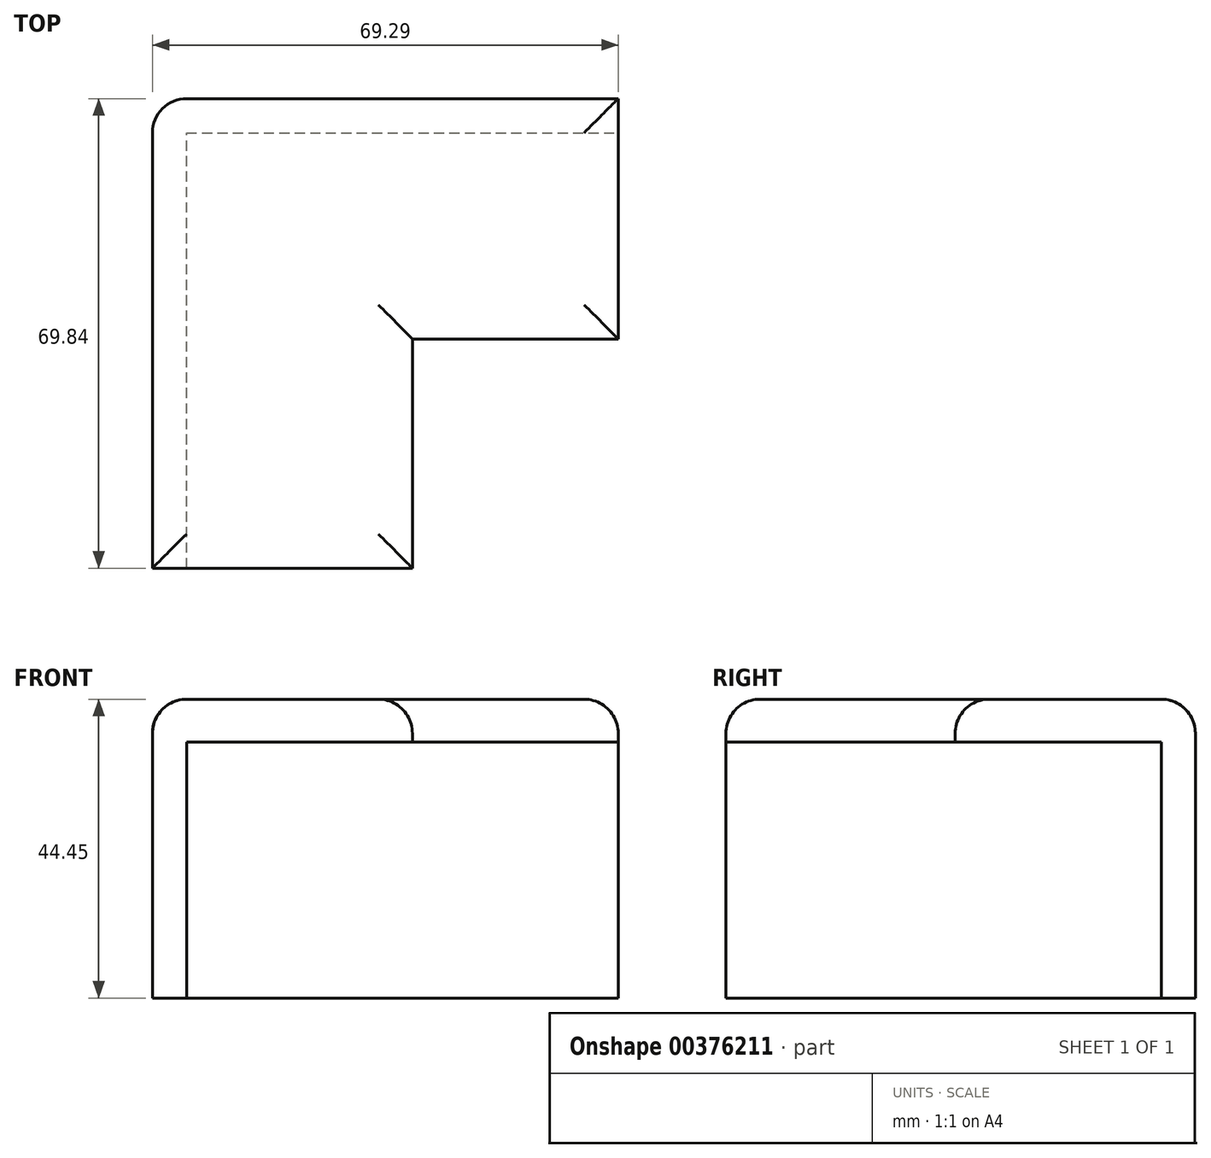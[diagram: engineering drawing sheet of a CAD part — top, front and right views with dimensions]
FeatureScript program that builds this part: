
annotation { "Feature Type Name" : "Feature", "Feature Type Description" : "" }
export const myFeature = defineFeature(function(context is Context, id is Id, definition is map)
    precondition{}
    {
        {
            var Q0;
            Q0=qCreatedBy(makeId("Top.planeOp"),FACE);
            var sketch = newSketch(context, id + "F0", { "sketchPlane" : qUnion([Q0])});
            skLineSegment(sketch, "E0", {"start": v(0, 0) * mm, "end": v(69.3, 0) * mm});
            skLineSegment(sketch, "E1", {"start": v(69.3, 0) * mm, "end": v(69.3, -35.75) * mm});
            skLineSegment(sketch, "E2", {"start": v(69.3, -35.75) * mm, "end": v(38.68, -35.75) * mm});
            skLineSegment(sketch, "E3", {"start": v(38.68, -35.75) * mm, "end": v(38.68, -69.84) * mm});
            skLineSegment(sketch, "E4", {"start": v(38.68, -69.84) * mm, "end": v(0, -69.84) * mm});
            skLineSegment(sketch, "E5", {"start": v(0, -69.84) * mm, "end": v(0, 0) * mm});
            skSolve(sketch);
        }
        {
            var Q0;
            Q0=makeQuery(id+"F0.imprint","IMPRINT",FACE,{"disambiguationData":[TD([[makeQuery(id+"F0.imprint","IMPRINT",EDGE,{"derivedFrom":sQuery(id+"F0.wireOp",EDGE,"E0")}),-1.0]])]});
            extrude(context, id + "F1", {"entities" : qUnion([Q0]), "depth" : 6.35 * mm});
        }
        {
            var Q0;
            Q0=makeQuery(id+"F1.opExtrude","CAP_FACE",FACE,{"disambiguationData":[OSD([sQuery(id+"F0.wireOp",EDGE,"E0"),sQuery(id+"F0.wireOp",EDGE,"E1"),sQuery(id+"F0.wireOp",EDGE,"E2"),sQuery(id+"F0.wireOp",EDGE,"E3"),sQuery(id+"F0.wireOp",EDGE,"E4"),sQuery(id+"F0.wireOp",EDGE,"E5")])],"isStart":true});
            var sketch = newSketch(context, id + "F2", { "sketchPlane" : qUnion([Q0])});
            skLineSegment(sketch, "E6.0", {"start": v(0, 69.84) * mm, "end": v(0, 0) * mm});
            skLineSegment(sketch, "E7.0", {"start": v(0, 0) * mm, "end": v(69.3, 0) * mm});
            skLineSegment(sketch, "E8.0", {"start": v(5.08, 5.08) * mm, "end": v(69.3, 5.08) * mm});
            skLineSegment(sketch, "E8.1", {"start": v(5.08, 69.84) * mm, "end": v(5.08, 5.08) * mm});
            skLineSegment(sketch, "E9", {"start": v(69.3, 0) * mm, "end": v(69.3, 5.08) * mm});
            skLineSegment(sketch, "E10", {"start": v(0, 69.84) * mm, "end": v(5.08, 69.84) * mm});
            skSolve(sketch);
        }
        {
            var Q0;
            Q0=makeQuery(id+"F2.imprint","IMPRINT",FACE,{"disambiguationData":[TD([[makeQuery(id+"F2.imprint","IMPRINT",EDGE,{"derivedFrom":sQuery(id+"F2.wireOp",EDGE,"E6.0")}),1.0]])]});
            extrude(context, id + "F3", {"entities" : qUnion([Q0]), "operationType" : NewBodyOperationType.ADD, "depth" : 38.1 * mm});
        }
        {
            var Q0;
            Q0=makeQuery(id+"F1.opExtrude","CAP_FACE",FACE,{"disambiguationData":[OSD([sQuery(id+"F0.wireOp",EDGE,"E0"),sQuery(id+"F0.wireOp",EDGE,"E1"),sQuery(id+"F0.wireOp",EDGE,"E2"),sQuery(id+"F0.wireOp",EDGE,"E3"),sQuery(id+"F0.wireOp",EDGE,"E4"),sQuery(id+"F0.wireOp",EDGE,"E5")])],"isStart":false});
            fillet(context, id + "F4", {"entities" : qUnion([Q0]), "radius" : 5.08 * mm, "tangentPropagation" : true, "allowEdgeOverflow" : false});
        }
        {
            var Q0;
            Q0=makeQuery(id+"F3.boolean.opBoolean","MERGE",EDGE,{"derivedFrom":[makeQuery(id+"F1.opExtrude","SWEPT_EDGE",EDGE,{"disambiguationData":[OSD([sQuery(id+"F0.wireOp",EDGE,"E0"),sQuery(id+"F0.wireOp",EDGE,"E5")])]}),makeQuery(id+"F3.opExtrude","SWEPT_EDGE",EDGE,{"disambiguationData":[OSD([sQuery(id+"F2.wireOp",EDGE,"E6.0"),sQuery(id+"F2.wireOp",EDGE,"E7.0")])]})]});
            fillet(context, id + "F5", {"entities" : qUnion([Q0]), "radius" : 5.08 * mm, "tangentPropagation" : true, "allowEdgeOverflow" : false});
        }
    });
